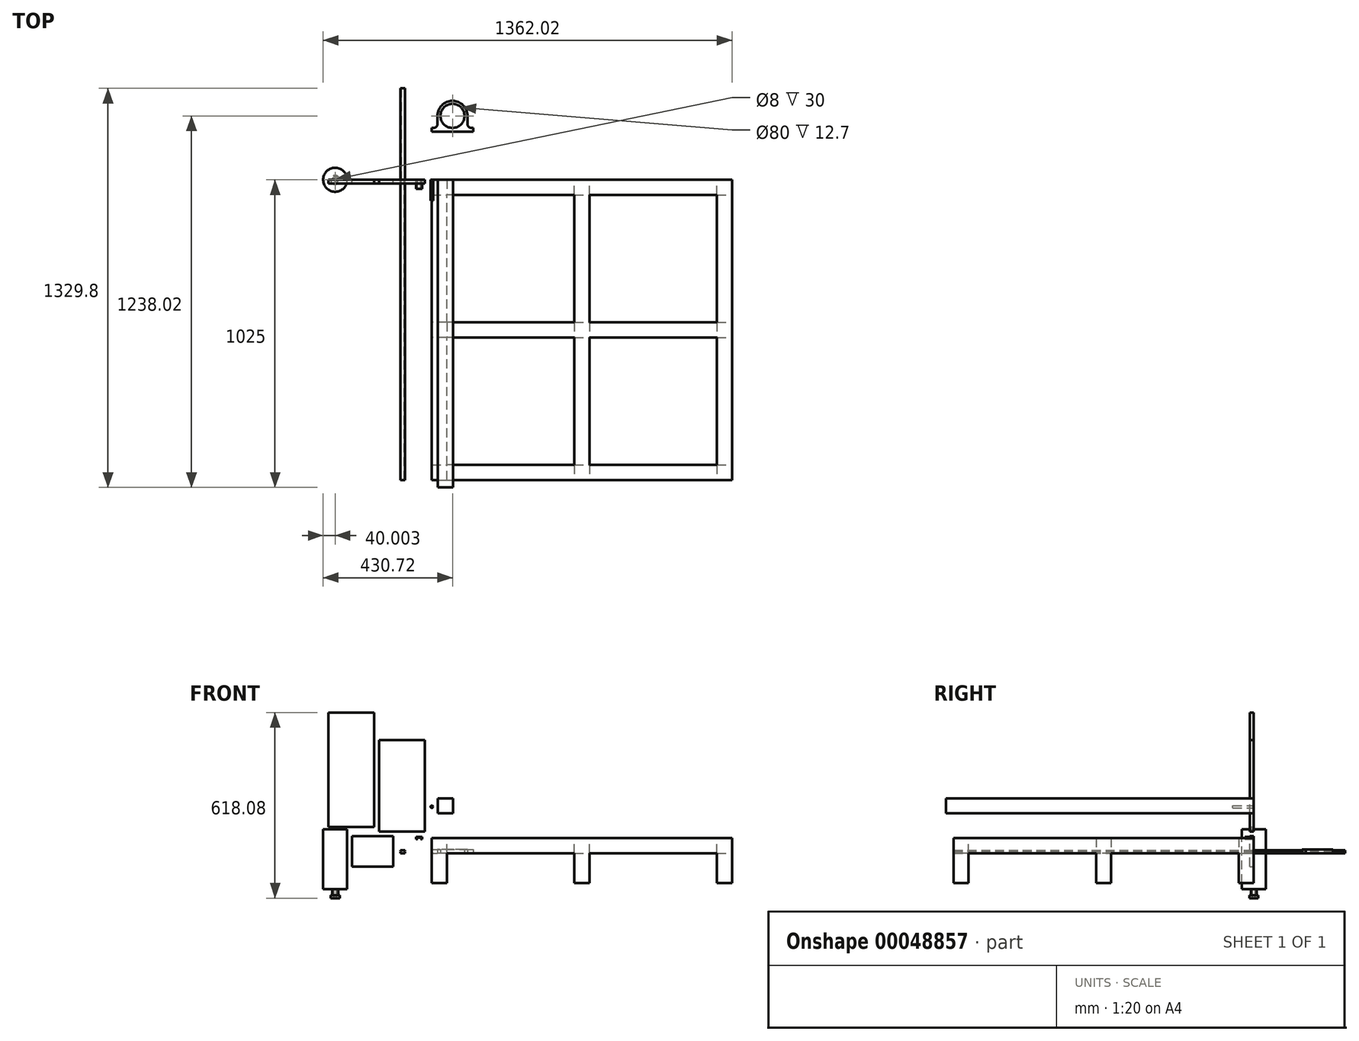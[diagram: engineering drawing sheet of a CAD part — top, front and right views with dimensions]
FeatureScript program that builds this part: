
annotation { "Feature Type Name" : "Feature", "Feature Type Description" : "" }
export const myFeature = defineFeature(function(context is Context, id is Id, definition is map)
    precondition{}
    {
        {
            var Q0;
            Q0=qCreatedBy(makeId("Front.planeOp"),FACE);
            var sketch = newSketch(context, id + "F0", { "sketchPlane" : qUnion([Q0])});
            skLineSegment(sketch, "E0.bottom", {"start": v(0, 0) * mm, "end": v(50, 0) * mm});
            skLineSegment(sketch, "E0.top", {"start": v(0, 50) * mm, "end": v(50, 50) * mm});
            skLineSegment(sketch, "E0.left", {"start": v(0, 0) * mm, "end": v(0, 50) * mm});
            skLineSegment(sketch, "E0.right", {"start": v(50, 0) * mm, "end": v(50, 50) * mm});
            skSolve(sketch);
        }
        {
            var Q0;
            Q0 = qSketchRegion(id + "F0", true);
            extrude(context, id + "F1", {"entities" : qUnion([Q0]), "depth" : 1000 * mm});
        }
        {
            var Q0;
            Q0=makeQuery(id+"F1.opExtrude","SWEPT_FACE",FACE,{"disambiguationData":[OSD([sQuery(id+"F0.wireOp",EDGE,"E0.right")])]});
            var sketch = newSketch(context, id + "F2", { "sketchPlane" : qUnion([Q0])});
            skLineSegment(sketch, "E1.bottom", {"start": v(-1000, 0) * mm, "end": v(-950, 0) * mm});
            skLineSegment(sketch, "E1.top", {"start": v(-1000, 50) * mm, "end": v(-950, 50) * mm});
            skLineSegment(sketch, "E1.left", {"start": v(-1000, 0) * mm, "end": v(-1000, 50) * mm});
            skLineSegment(sketch, "E1.right", {"start": v(-950, 0) * mm, "end": v(-950, 50) * mm});
            skLineSegment(sketch, "E2.rect.bottom", {"start": v(-475, 50) * mm, "end": v(-525, 50) * mm});
            skLineSegment(sketch, "E2.rect.top", {"start": v(-475, 0) * mm, "end": v(-525, 0) * mm});
            skLineSegment(sketch, "E2.rect.left", {"start": v(-475, 50) * mm, "end": v(-475, 0) * mm});
            skLineSegment(sketch, "E2.rect.right", {"start": v(-525, 50) * mm, "end": v(-525, 0) * mm});
            skPoint(sketch, "E2.rect.middle", {"position": v(-500, 25) * mm});
            skPoint(sketch, "E2.rect.middle.positionSnap0", {"position": v(-500, 50) * mm});
            skPoint(sketch, "E2.rect.middle.positionSnap1", {"position": v(-1000, 25) * mm});
            skPoint(sketch, "E2.rect.centerSnap0", {"position": v(-500, 50) * mm});
            skPoint(sketch, "E2.rect.centerSnap1", {"position": v(-1000, 25) * mm});
            skLineSegment(sketch, "E3.bottom", {"start": v(0, 50) * mm, "end": v(-50, 50) * mm});
            skLineSegment(sketch, "E3.top", {"start": v(0, 0) * mm, "end": v(-50, 0) * mm});
            skLineSegment(sketch, "E3.left", {"start": v(0, 50) * mm, "end": v(0, 0) * mm});
            skLineSegment(sketch, "E3.right", {"start": v(-50, 50) * mm, "end": v(-50, 0) * mm});
            skSolve(sketch);
        }
        {
            var Q0;
            Q0=makeQuery(id+"F2.imprint","IMPRINT",FACE,{"disambiguationData":[TD([[makeQuery(id+"F2.imprint","IMPRINT",EDGE,{"derivedFrom":sQuery(id+"F2.wireOp",EDGE,"E2.rect.bottom")}),-1.0]])]});
            var Q1;
            Q1=makeQuery(id+"F2.imprint","IMPRINT",FACE,{"disambiguationData":[TD([[makeQuery(id+"F2.imprint","IMPRINT",EDGE,{"derivedFrom":sQuery(id+"F2.wireOp",EDGE,"E1.bottom")}),1.0]])]});
            var Q2;
            Q2=makeQuery(id+"F2.imprint","IMPRINT",FACE,{"disambiguationData":[TD([[makeQuery(id+"F2.imprint","IMPRINT",EDGE,{"derivedFrom":sQuery(id+"F2.wireOp",EDGE,"E3.bottom")}),-1.0]])]});
            extrude(context, id + "F3", {"entities" : qUnion([Q0, Q1, Q2]), "operationType" : NewBodyOperationType.ADD, "depth" : 450 * mm});
        }
        {
            var Q0;
            Q0=makeQuery(id+"F3.opExtrude","SWEPT_FACE",FACE,{"disambiguationData":[OSD([sQuery(id+"F2.wireOp",EDGE,"E1.right")])]});
            var sketch = newSketch(context, id + "F4", { "sketchPlane" : qUnion([Q0])});
            skLineSegment(sketch, "E4.bottom", {"start": v(-500, 0) * mm, "end": v(-475, 0) * mm});
            skLineSegment(sketch, "E4.top", {"start": v(-500, 50) * mm, "end": v(-475, 50) * mm});
            skLineSegment(sketch, "E4.left", {"start": v(-500, 0) * mm, "end": v(-500, 50) * mm});
            skLineSegment(sketch, "E4.right", {"start": v(-475, 0) * mm, "end": v(-475, 50) * mm});
            skSolve(sketch);
        }
        {
            var Q0;
            Q0 = qSketchRegion(id + "F4", true);
            extrude(context, id + "F5", {"entities" : qUnion([Q0]), "operationType" : NewBodyOperationType.ADD, "depth" : 900 * mm});
        }
        {
            var Q0;
            Q0=makeQuery(id+"F1.opExtrude","SWEPT_BODY",BODY,{"disambiguationData":[OSD([sQuery(id+"F0.wireOp",EDGE,"E0.bottom"),sQuery(id+"F0.wireOp",EDGE,"E0.top"),sQuery(id+"F0.wireOp",EDGE,"E0.left"),sQuery(id+"F0.wireOp",EDGE,"E0.right")])]});
            var Q1;
            Q1=makeQuery(id+"F5.boolean.opBoolean","MERGE",FACE,{"derivedFrom":[makeQuery(id+"F3.opExtrude","CAP_FACE",FACE,{"disambiguationData":[OSD([sQuery(id+"F2.wireOp",EDGE,"E1.bottom"),sQuery(id+"F2.wireOp",EDGE,"E1.top"),sQuery(id+"F2.wireOp",EDGE,"E1.left"),sQuery(id+"F2.wireOp",EDGE,"E1.right")])],"isStart":false}),makeQuery(id+"F3.opExtrude","CAP_FACE",FACE,{"disambiguationData":[OSD([sQuery(id+"F2.wireOp",EDGE,"E2.rect.bottom"),sQuery(id+"F2.wireOp",EDGE,"E2.rect.top"),sQuery(id+"F2.wireOp",EDGE,"E2.rect.left"),sQuery(id+"F2.wireOp",EDGE,"E2.rect.right")])],"isStart":false}),makeQuery(id+"F3.opExtrude","CAP_FACE",FACE,{"disambiguationData":[OSD([sQuery(id+"F2.wireOp",EDGE,"E3.bottom"),sQuery(id+"F2.wireOp",EDGE,"E3.top"),sQuery(id+"F2.wireOp",EDGE,"E3.left"),sQuery(id+"F2.wireOp",EDGE,"E3.right")])],"isStart":false}),makeQuery(id+"F5.opExtrude","SWEPT_FACE",FACE,{"disambiguationData":[OSD([sQuery(id+"F4.wireOp",EDGE,"E4.left")])]})]});
            mirror(context, id + "F6", {"operationType" : NewBodyOperationType.ADD, "entities" : qUnion([Q0]), "mirrorPlane" : qUnion([Q1])});
        }
        {
            var Q0;
            {var subQ0=makeQuery(id+"F5.boolean.opBoolean","MERGE",FACE,{"derivedFrom":[makeQuery(id+"F3.boolean.opBoolean","MERGE",FACE,{"derivedFrom":[makeQuery(id+"F1.opExtrude","SWEPT_FACE",FACE,{"disambiguationData":[OSD([sQuery(id+"F0.wireOp",EDGE,"E0.bottom")])]}),makeQuery(id+"F3.opExtrude","SWEPT_FACE",FACE,{"disambiguationData":[OSD([sQuery(id+"F2.wireOp",EDGE,"E1.bottom")])]}),makeQuery(id+"F3.opExtrude","SWEPT_FACE",FACE,{"disambiguationData":[OSD([sQuery(id+"F2.wireOp",EDGE,"E2.rect.top")])]}),makeQuery(id+"F3.opExtrude","SWEPT_FACE",FACE,{"disambiguationData":[OSD([sQuery(id+"F2.wireOp",EDGE,"E3.top")])]})]}),makeQuery(id+"F5.opExtrude","SWEPT_FACE",FACE,{"disambiguationData":[OSD([sQuery(id+"F4.wireOp",EDGE,"E4.bottom")])]})]});Q0=makeQuery(id+"F6.boolean.opBoolean","MERGE",FACE,{"derivedFrom":[subQ0,makeQuery(id+"F6.opPattern","COPY",FACE,{"derivedFrom":subQ0,"instanceName":"1"})]});}
            var sketch = newSketch(context, id + "F7", { "sketchPlane" : qUnion([Q0])});
            skLineSegment(sketch, "E5.bottom", {"start": v(0, 1000) * mm, "end": v(50, 1000) * mm});
            skLineSegment(sketch, "E5.top", {"start": v(0, 950) * mm, "end": v(50, 950) * mm});
            skLineSegment(sketch, "E5.left", {"start": v(0, 1000) * mm, "end": v(0, 950) * mm});
            skLineSegment(sketch, "E5.right", {"start": v(50, 1000) * mm, "end": v(50, 950) * mm});
            skLineSegment(sketch, "E6.bottom", {"start": v(950, 950) * mm, "end": v(1000, 950) * mm});
            skLineSegment(sketch, "E6.top", {"start": v(950, 1000) * mm, "end": v(1000, 1000) * mm});
            skLineSegment(sketch, "E6.left", {"start": v(950, 950) * mm, "end": v(950, 1000) * mm});
            skLineSegment(sketch, "E6.right", {"start": v(1000, 950) * mm, "end": v(1000, 1000) * mm});
            skLineSegment(sketch, "E7.bottom", {"start": v(475, 475) * mm, "end": v(525, 475) * mm});
            skLineSegment(sketch, "E7.top", {"start": v(475, 525) * mm, "end": v(525, 525) * mm});
            skLineSegment(sketch, "E7.left", {"start": v(475, 475) * mm, "end": v(475, 525) * mm});
            skLineSegment(sketch, "E7.right", {"start": v(525, 475) * mm, "end": v(525, 525) * mm});
            skLineSegment(sketch, "E8.bottom", {"start": v(950, 50) * mm, "end": v(1000, 50) * mm});
            skLineSegment(sketch, "E8.top", {"start": v(950, 0) * mm, "end": v(1000, 0) * mm});
            skLineSegment(sketch, "E8.left", {"start": v(950, 50) * mm, "end": v(950, 0) * mm});
            skLineSegment(sketch, "E8.right", {"start": v(1000, 50) * mm, "end": v(1000, 0) * mm});
            skLineSegment(sketch, "E9.bottom", {"start": v(0, 0) * mm, "end": v(50, 0) * mm});
            skLineSegment(sketch, "E9.top", {"start": v(0, 50) * mm, "end": v(50, 50) * mm});
            skLineSegment(sketch, "E9.left", {"start": v(0, 0) * mm, "end": v(0, 50) * mm});
            skLineSegment(sketch, "E9.right", {"start": v(50, 0) * mm, "end": v(50, 50) * mm});
            skLineSegment(sketch, "E10.bottom", {"start": v(50, 475) * mm, "end": v(0, 475) * mm});
            skLineSegment(sketch, "E10.top", {"start": v(50, 525) * mm, "end": v(0, 525) * mm});
            skLineSegment(sketch, "E10.left", {"start": v(50, 475) * mm, "end": v(50, 525) * mm});
            skLineSegment(sketch, "E10.right", {"start": v(0, 475) * mm, "end": v(0, 525) * mm});
            skLineSegment(sketch, "E11.bottom", {"start": v(950, 475) * mm, "end": v(1000, 475) * mm});
            skLineSegment(sketch, "E11.top", {"start": v(950, 525) * mm, "end": v(1000, 525) * mm});
            skLineSegment(sketch, "E11.left", {"start": v(950, 475) * mm, "end": v(950, 525) * mm});
            skLineSegment(sketch, "E11.right", {"start": v(1000, 475) * mm, "end": v(1000, 525) * mm});
            skLineSegment(sketch, "E12.bottom", {"start": v(475, 50) * mm, "end": v(525, 50) * mm});
            skLineSegment(sketch, "E12.top", {"start": v(475, 0) * mm, "end": v(525, 0) * mm});
            skLineSegment(sketch, "E12.left", {"start": v(475, 50) * mm, "end": v(475, 0) * mm});
            skLineSegment(sketch, "E12.right", {"start": v(525, 50) * mm, "end": v(525, 0) * mm});
            skLineSegment(sketch, "E13.bottom", {"start": v(475, 950) * mm, "end": v(525, 950) * mm});
            skLineSegment(sketch, "E13.top", {"start": v(475, 1000) * mm, "end": v(525, 1000) * mm});
            skLineSegment(sketch, "E13.left", {"start": v(475, 950) * mm, "end": v(475, 1000) * mm});
            skLineSegment(sketch, "E13.right", {"start": v(525, 950) * mm, "end": v(525, 1000) * mm});
            skSolve(sketch);
        }
        {
            var Q0;
            Q0=makeQuery(id+"F7.imprint","IMPRINT",FACE,{"disambiguationData":[TD([[makeQuery(id+"F7.imprint","IMPRINT",EDGE,{"derivedFrom":sQuery(id+"F7.wireOp",EDGE,"E5.bottom")}),-1.0]])]});
            var Q1;
            Q1=makeQuery(id+"F7.imprint","IMPRINT",FACE,{"disambiguationData":[TD([[makeQuery(id+"F7.imprint","IMPRINT",EDGE,{"derivedFrom":sQuery(id+"F7.wireOp",EDGE,"E6.bottom")}),1.0]])]});
            var Q2;
            Q2=makeQuery(id+"F7.imprint","IMPRINT",FACE,{"disambiguationData":[TD([[makeQuery(id+"F7.imprint","IMPRINT",EDGE,{"derivedFrom":sQuery(id+"F7.wireOp",EDGE,"E8.bottom")}),-1.0]])]});
            var Q3;
            Q3=makeQuery(id+"F7.imprint","IMPRINT",FACE,{"disambiguationData":[TD([[makeQuery(id+"F7.imprint","IMPRINT",EDGE,{"derivedFrom":sQuery(id+"F7.wireOp",EDGE,"E9.bottom")}),1.0]])]});
            var Q4;
            Q4=makeQuery(id+"F7.imprint","IMPRINT",FACE,{"disambiguationData":[TD([[makeQuery(id+"F7.imprint","IMPRINT",EDGE,{"derivedFrom":sQuery(id+"F7.wireOp",EDGE,"E10.bottom")}),-1.0]])]});
            var Q5;
            Q5=makeQuery(id+"F7.imprint","IMPRINT",FACE,{"disambiguationData":[TD([[makeQuery(id+"F7.imprint","IMPRINT",EDGE,{"derivedFrom":sQuery(id+"F7.wireOp",EDGE,"E11.bottom")}),1.0]])]});
            var Q6;
            Q6=makeQuery(id+"F7.imprint","IMPRINT",FACE,{"disambiguationData":[TD([[makeQuery(id+"F7.imprint","IMPRINT",EDGE,{"derivedFrom":sQuery(id+"F7.wireOp",EDGE,"E12.bottom")}),-1.0]])]});
            var Q7;
            Q7=makeQuery(id+"F7.imprint","IMPRINT",FACE,{"disambiguationData":[TD([[makeQuery(id+"F7.imprint","IMPRINT",EDGE,{"derivedFrom":sQuery(id+"F7.wireOp",EDGE,"E7.bottom")}),1.0]])]});
            var Q8;
            Q8=makeQuery(id+"F7.imprint","IMPRINT",FACE,{"disambiguationData":[TD([[makeQuery(id+"F7.imprint","IMPRINT",EDGE,{"derivedFrom":sQuery(id+"F7.wireOp",EDGE,"E13.bottom")}),1.0]])]});
            extrude(context, id + "F8", {"entities" : qUnion([Q0, Q1, Q2, Q3, Q4, Q5, Q6, Q7, Q8]), "operationType" : NewBodyOperationType.ADD, "depth" : 100 * mm});
        }
        {
            var Q0;
            Q0=qCreatedBy(makeId("Front.planeOp"),FACE);
            var sketch = newSketch(context, id + "F9", { "sketchPlane" : qUnion([Q0])});
            skLineSegment(sketch, "E14.bottom", {"start": v(-104.8, 0) * mm, "end": v(-89.8, 0) * mm});
            skLineSegment(sketch, "E14.top", {"start": v(-104.8, 10) * mm, "end": v(-89.8, 10) * mm});
            skLineSegment(sketch, "E14.left", {"start": v(-104.8, 0) * mm, "end": v(-104.8, 5) * mm});
            skLineSegment(sketch, "E14.right", {"start": v(-89.8, 0) * mm, "end": v(-89.8, 5) * mm});
            skLineSegment(sketch, "E15", {"start": v(-104.8, 7.5) * mm, "end": v(-102.3, 6.25) * mm});
            skLineSegment(sketch, "E16", {"start": v(-102.3, 6.25) * mm, "end": v(-104.8, 5) * mm});
            skLineSegment(sketch, "E17.MirrorCS", {"start": v(-92.3, 6.25) * mm, "end": v(-89.8, 5) * mm});
            skLineSegment(sketch, "E18.MirrorCS", {"start": v(-89.8, 7.5) * mm, "end": v(-92.3, 6.25) * mm});
            skLineSegment(sketch, "E19.trimOffspring", {"start": v(-104.8, 7.5) * mm, "end": v(-104.8, 10) * mm});
            skLineSegment(sketch, "E20.trimOffspring", {"start": v(-89.8, 7.5) * mm, "end": v(-89.8, 10) * mm});
            skSolve(sketch);
        }
        {
            var Q0;
            Q0 = qSketchRegion(id + "F9", true);
            extrude(context, id + "F10", {"entities" : qUnion([Q0]), "depth" : 1000 * mm});
        }
        {
            var Q0;
            Q0=qCreatedBy(makeId("Front.planeOp"),FACE);
            var sketch = newSketch(context, id + "F11", { "sketchPlane" : qUnion([Q0])});
            skLineSegment(sketch, "E21.bottom", {"start": v(-191.81, 87.28) * mm, "end": v(-344.21, 87.28) * mm});
            skLineSegment(sketch, "E21.top", {"start": v(-191.81, 468.28) * mm, "end": v(-344.21, 468.28) * mm});
            skLineSegment(sketch, "E21.left", {"start": v(-191.81, 87.28) * mm, "end": v(-191.81, 468.28) * mm});
            skLineSegment(sketch, "E21.right", {"start": v(-344.21, 87.28) * mm, "end": v(-344.21, 468.28) * mm});
            skSolve(sketch);
        }
        {
            var Q0;
            Q0 = qSketchRegion(id + "F11", true);
            extrude(context, id + "F12", {"entities" : qUnion([Q0]), "depth" : 12.7 * mm});
        }
        {
            var Q0;
            Q0=qCreatedBy(makeId("Front.planeOp"),FACE);
            var sketch = newSketch(context, id + "F13", { "sketchPlane" : qUnion([Q0])});
            skLineSegment(sketch, "E22.bottom", {"start": v(-32.18, 46.35) * mm, "end": v(-34.68, 46.35) * mm});
            skLineSegment(sketch, "E22.top", {"start": v(-32.18, 53.85) * mm, "end": v(-52.18, 53.85) * mm});
            skLineSegment(sketch, "E22.left", {"start": v(-32.18, 46.35) * mm, "end": v(-32.18, 53.85) * mm});
            skLineSegment(sketch, "E22.right", {"start": v(-52.18, 46.35) * mm, "end": v(-52.18, 53.85) * mm});
            skLineSegment(sketch, "E23.top", {"start": v(-34.68, 51.35) * mm, "end": v(-49.68, 51.35) * mm});
            skLineSegment(sketch, "E23.left", {"start": v(-34.68, 48.85) * mm, "end": v(-34.68, 51.35) * mm});
            skLineSegment(sketch, "E24", {"start": v(-34.68, 46.35) * mm, "end": v(-37.18, 47.6) * mm});
            skLineSegment(sketch, "E25", {"start": v(-37.18, 47.6) * mm, "end": v(-34.68, 48.85) * mm});
            skLineSegment(sketch, "E26.MirrorCS", {"start": v(-49.68, 46.35) * mm, "end": v(-47.18, 47.6) * mm});
            skLineSegment(sketch, "E27.MirrorCS", {"start": v(-47.18, 47.6) * mm, "end": v(-49.68, 48.85) * mm});
            skLineSegment(sketch, "E28.trimOffspring", {"start": v(-49.68, 46.35) * mm, "end": v(-52.18, 46.35) * mm});
            skLineSegment(sketch, "E29", {"start": v(-49.68, 48.85) * mm, "end": v(-49.68, 51.35) * mm});
            skSolve(sketch);
        }
        {
            var Q0;
            Q0 = qSketchRegion(id + "F13", true);
            extrude(context, id + "F14", {"entities" : qUnion([Q0]), "depth" : 30 * mm});
        }
        {
            var Q0;
            Q0=qCreatedBy(makeId("Front.planeOp"),FACE);
            var sketch = newSketch(context, id + "F15", { "sketchPlane" : qUnion([Q0])});
            skLineSegment(sketch, "E30.bottom", {"start": v(70.08, 132.5) * mm, "end": v(20.08, 132.5) * mm});
            skLineSegment(sketch, "E30.top", {"start": v(70.08, 182.5) * mm, "end": v(20.08, 182.5) * mm});
            skLineSegment(sketch, "E30.left", {"start": v(70.08, 132.5) * mm, "end": v(70.08, 182.5) * mm});
            skLineSegment(sketch, "E30.right", {"start": v(20.08, 132.5) * mm, "end": v(20.08, 182.5) * mm});
            skSolve(sketch);
        }
        {
            var Q0;
            Q0 = qSketchRegion(id + "F15", true);
            extrude(context, id + "F16", {"entities" : qUnion([Q0]), "depth" : 1025 * mm});
        }
        {
            var Q0;
            Q0=qCreatedBy(makeId("Front.planeOp"),FACE);
            var sketch = newSketch(context, id + "F17", { "sketchPlane" : qUnion([Q0])});
            skLineSegment(sketch, "E31.bottom", {"start": v(-23.77, 71.93) * mm, "end": v(-176.17, 71.93) * mm});
            skLineSegment(sketch, "E31.top", {"start": v(-23.77, 376.73) * mm, "end": v(-176.17, 376.73) * mm});
            skLineSegment(sketch, "E31.left", {"start": v(-23.77, 71.93) * mm, "end": v(-23.77, 376.73) * mm});
            skLineSegment(sketch, "E31.right", {"start": v(-176.17, 71.93) * mm, "end": v(-176.17, 376.73) * mm});
            skSolve(sketch);
        }
        {
            var Q0;
            Q0 = qSketchRegion(id + "F17", true);
            extrude(context, id + "F18", {"entities" : qUnion([Q0]), "depth" : 12.7 * mm});
        }
        {
            var Q0;
            Q0=makeQuery(id+"F10.opExtrude","CAP_FACE",FACE,{"disambiguationData":[OSD([sQuery(id+"F9.wireOp",EDGE,"E14.bottom"),sQuery(id+"F9.wireOp",EDGE,"E14.top"),sQuery(id+"F9.wireOp",EDGE,"E14.left"),sQuery(id+"F9.wireOp",EDGE,"E14.right"),sQuery(id+"F9.wireOp",EDGE,"E15"),sQuery(id+"F9.wireOp",EDGE,"E16"),sQuery(id+"F9.wireOp",EDGE,"E17.MirrorCS"),sQuery(id+"F9.wireOp",EDGE,"E18.MirrorCS"),sQuery(id+"F9.wireOp",EDGE,"E19.trimOffspring"),sQuery(id+"F9.wireOp",EDGE,"E20.trimOffspring")])],"isStart":true});
            extrude(context, id + "F19", {"entities" : qUnion([Q0]), "depth" : 304.8 * mm});
        }
        {
            var Q0;
            Q0=qCreatedBy(makeId("Front.planeOp"),FACE);
            var sketch = newSketch(context, id + "F20", { "sketchPlane" : qUnion([Q0])});
            skLineSegment(sketch, "E32.bottom", {"start": v(-128.67, -44.49) * mm, "end": v(-266.07, -44.49) * mm});
            skLineSegment(sketch, "E32.top", {"start": v(-128.67, 57.11) * mm, "end": v(-266.07, 57.11) * mm});
            skLineSegment(sketch, "E32.left", {"start": v(-128.67, -44.49) * mm, "end": v(-128.67, 57.11) * mm});
            skLineSegment(sketch, "E32.right", {"start": v(-266.07, -44.49) * mm, "end": v(-266.07, 57.11) * mm});
            skSolve(sketch);
        }
        {
            var Q0;
            Q0 = qSketchRegion(id + "F20", true);
            extrude(context, id + "F21", {"entities" : qUnion([Q0]), "depth" : 12.7 * mm});
        }
        {
            var Q0;
            Q0=qCreatedBy(makeId("Top.planeOp"),FACE);
            var sketch = newSketch(context, id + "F22", { "sketchPlane" : qUnion([Q0])});
            skLineSegment(sketch, "E33.bottom", {"start": v(0, 160.32) * mm, "end": v(137.4, 160.32) * mm});
            skLineSegment(sketch, "E33.top", {"start": v(0, 173.02) * mm, "end": v(18.7, 173.02) * mm});
            skLineSegment(sketch, "E33.left", {"start": v(0, 160.32) * mm, "end": v(0, 173.02) * mm});
            skLineSegment(sketch, "E33.right", {"start": v(137.4, 160.32) * mm, "end": v(137.4, 173.02) * mm});
            skLineSegment(sketch, "E34.top", {"start": v(68.7, 263.02) * mm, "end": v(68.7, 263.02) * mm});
            skLineSegment(sketch, "E34.left", {"start": v(18.7, 173.02) * mm, "end": v(18.7, 213.02) * mm});
            skLineSegment(sketch, "E34.right", {"start": v(118.7, 173.02) * mm, "end": v(118.7, 213.02) * mm});
            skPoint(sketch, "E35.centerSnap0", {"position": v(18.7, 218.02) * mm});
            skPoint(sketch, "E35.centerSnap1", {"position": v(68.7, 263.02) * mm});
            skLineSegment(sketch, "E36.trimOffspring", {"start": v(118.7, 173.02) * mm, "end": v(137.4, 173.02) * mm});
            skPoint(sketch, "E37.visualSharp", {"position": v(18.7, 263.02) * mm});
            skArc(sketch, "E37.filletArc", {"start": v(68.7, 263.02) * mm, "mid": v(33.34, 248.38) * mm, "end": v(18.7, 213.02) * mm});
            skPoint(sketch, "E38.visualSharp", {"position": v(118.7, 263.02) * mm});
            skArc(sketch, "E38.filletArc", {"start": v(118.7, 213.02) * mm, "mid": v(104.06, 248.38) * mm, "end": v(68.7, 263.02) * mm});
            skCircle(sketch, "E39", {"center": v(68.7, 213.02) * mm, "radius": 40 * mm});
            skSolve(sketch);
        }
        {
            var Q0;
            Q0=makeQuery(id+"F22.imprint","IMPRINT",FACE,{"disambiguationData":[TD([[makeQuery(id+"F22.imprint","IMPRINT",EDGE,{"derivedFrom":sQuery(id+"F22.wireOp",EDGE,"E33.bottom")}),1.0]])]});
            extrude(context, id + "F23", {"entities" : qUnion([Q0]), "depth" : 12.7 * mm});
        }
        {
            var Q0;
            Q0=makeQuery(id+"F23.opExtrude","SWEPT_EDGE",EDGE,{"disambiguationData":[OSD([sQuery(id+"F22.wireOp",EDGE,"E34.right"),sQuery(id+"F22.wireOp",EDGE,"E36.trimOffspring")])]});
            var Q1;
            Q1=makeQuery(id+"F23.opExtrude","SWEPT_EDGE",EDGE,{"disambiguationData":[OSD([sQuery(id+"F22.wireOp",EDGE,"E33.top"),sQuery(id+"F22.wireOp",EDGE,"E34.left")])]});
            fillet(context, id + "F24", {"entities" : qUnion([Q0, Q1]), "radius" : 12.7 * mm, "tangentPropagation" : true, "allowEdgeOverflow" : false});
        }
        {
            var Q0;
            Q0=qCreatedBy(makeId("Front.planeOp"),FACE);
            var sketch = newSketch(context, id + "F25", { "sketchPlane" : qUnion([Q0])});
            skLineSegment(sketch, "E40", {"start": v(-326.02, -149.8) * mm, "end": v(-337.02, -149.8) * mm});
            skLineSegment(sketch, "E41", {"start": v(-337.02, -149.8) * mm, "end": v(-337.02, -139.8) * mm});
            skLineSegment(sketch, "E42", {"start": v(-337.02, -139.8) * mm, "end": v(-332.02, -139.8) * mm});
            skLineSegment(sketch, "E43", {"start": v(-332.02, -139.8) * mm, "end": v(-332.02, -119.8) * mm});
            skLineSegment(sketch, "E44", {"start": v(-332.02, -119.8) * mm, "end": v(-362.02, -119.8) * mm});
            skLineSegment(sketch, "E45", {"start": v(-362.02, -119.8) * mm, "end": v(-362.02, 80.2) * mm});
            skLineSegment(sketch, "E46", {"start": v(-362.02, 80.2) * mm, "end": v(-322.02, 80.2) * mm});
            skLineSegment(sketch, "E47", {"start": v(-322.02, 80.2) * mm, "end": v(-322.02, -119.8) * mm});
            skLineSegment(sketch, "E48", {"start": v(-322.02, -119.8) * mm, "end": v(-326.02, -119.8) * mm});
            skLineSegment(sketch, "E49", {"start": v(-326.02, -119.8) * mm, "end": v(-326.02, -149.8) * mm});
            skSolve(sketch);
        }
        {
            var Q0;
            Q0=makeQuery(id+"F25.imprint","IMPRINT",FACE,{"disambiguationData":[TD([[makeQuery(id+"F25.imprint","IMPRINT",EDGE,{"derivedFrom":sQuery(id+"F25.wireOp",EDGE,"E40")}),-1.0]])]});
            var Q1;
            Q1=sQuery(id+"F25.wireOp",EDGE,"E47");
            revolve(context, id + "F26", {"entities" : qUnion([Q0]), "axis" : qUnion([Q1]), "revolveType" : RevolveType.FULL});
        }
        {
            var Q0;
            Q0=qCreatedBy(makeId("Front.planeOp"),FACE);
            var sketch = newSketch(context, id + "F27", { "sketchPlane" : qUnion([Q0])});
            skCircle(sketch, "E50", {"center": v(0, 154.57) * mm, "radius": 4 * mm});
            skSolve(sketch);
        }
        {
            var Q0;
            Q0 = qSketchRegion(id + "F27", true);
            extrude(context, id + "F28", {"entities" : qUnion([Q0]), "depth" : 70 * mm});
        }
    });
